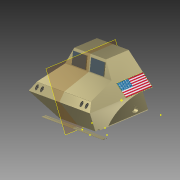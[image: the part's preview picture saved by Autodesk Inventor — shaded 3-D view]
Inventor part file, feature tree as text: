
AUTODESK INVENTOR PART (.ipt)
format: ipt  version: 2015 (Build 190159000, 159)  size: 406,016 bytes
history: native  units: in
note: dims shown in document units (in); Inventor stores cm internally (conversion verified against a paired STEP export)
features: sketch x21, extrude x9, plane x7, mirror x5, chamfer x4, other x3, fillet x1, hole x1, projected_geometry x1
ambient origin geometry x8: Origin, YZ Plane, XZ Plane, XY Plane, X Axis, Y Axis, Z Axis, Center Point
bodies: Solid1 (feature_tree)
feature tree (52):
  extrude  "Extrusion1"  Depth=3.06in
  extrude  "Extrusion2"  Depth=6.75in
  chamfer  "Chamfer1"  Distance=2.625in
  chamfer  "Chamfer2"  Distance=1.625in Angle=45.0deg
  extrude  "Extrusion3"  Depth=6.75in TaperAngle=0.0deg
  chamfer  "Chamfer3"  Distance=1.435in Angle=45.0deg
  chamfer  "Chamfer4"  Distance=1.435in Angle=45.0deg
  plane  "Work Plane1"
  extrude  "Extrusion4"  Depth=0.737in
  sketch  "Sketch5"  dims[d22=-1.38in d23=0.737in]
  plane  "Work Plane2"
  mirror  "Mirror1"
  extrude  "Extrusion5"  TaperAngle=90.0deg  [1 undecoded]
  mirror  "Mirror2"
  sketch  "Sketch7"  dims[d27=1.375in d28=1.375in d29=0.0in]
  sketch  "Sketch8"  dims[d30=1.516in d31=0.25in]
  sketch  "Sketch9"  dims[d32=0.36in d33=0.4in d34=0.0in d44=0.68in]
  other  "Work Point1"
  mirror  "Mirror3"
  plane  "Work Plane4"
  plane  "Work Plane5"
  plane  "Work Plane6"
  sketch  "Sketch10"  dims[d45=0.68in d51=0.05in d52=0.0in]
  sketch  "Sketch11"  dims[d53=2.4in d54=0.93in]
  sketch  "Sketch12"  dims[d55=0.795in]
  sketch  "Sketch13"  dims[d56=1.065in]
  extrude  "Extrusion6"  Depth=1.375in TaperAngle=0.0deg
  mirror  "Mirror4"
  sketch  "Sketch15"  dims[d59=0.2in]
  extrude  "Extrusion7"  Depth=0.25in
  extrude  "Extrusion8"  Depth=0.4in TaperAngle=0.0deg
  fillet  "Fillet1"  Radius=0.68in
  plane  "Work Plane7"
  sketch  "Sketch18"  dims[d62=1.0in]
  extrude  "Extrusion9"  Depth=0.05in TaperAngle=0.0deg
  sketch  "Sketch20"  dims[d69=1.0in]
  hole  "Hole4"  [1 undecoded]
  mirror  "Mirror6"
  sketch  "Sketch1"  dims[d0=3.17in d1=3.06in]
  sketch  "Sketch2"  dims[d2=6.75in d3=0.0in d4=0.5in]
  sketch  "Sketch3"  dims[d5=0.5in d6=2.625in d7=0.0in d8=1.625in d9=0.125in d10=45.0deg]
  sketch  "Sketch4"  dims[d11=1.625in d12=0.125in d13=45.0deg d14=6.75in d15=0.0in d16=1.435in d17=0.125in d18=45.0deg d19=1.435in d20=0.125in d21=45.0deg]
  projected_geometry  "Projected Loop1"
  plane  "Work Plane3"
  sketch  "Sketch6"  dims[d24=1.375in d25=0.0in d26=90.0deg]
  other  "Work Point2"
  sketch  "Sketch14"  dims[d57=0.57in d58=0.0in]
  other  "Image1"
  sketch  "Sketch16"  dims[d60=0.05in d61=0.0in]
  sketch  "Sketch17"  dims[d83=0.307in d84=0.75in d85=0.375in d86=0.25in d87=0.5635in d88=0.4in d89=0.8108in]
  sketch  "Sketch19"  dims[d63=1.0in]
  sketch  "Sketch24"  dims[d70=1.0in]
note: 2 required parameter values undecoded (feature->parameter linkage not recoverable at this tier; creation-order binding heuristic only, values carry confidence <= 0.55)
